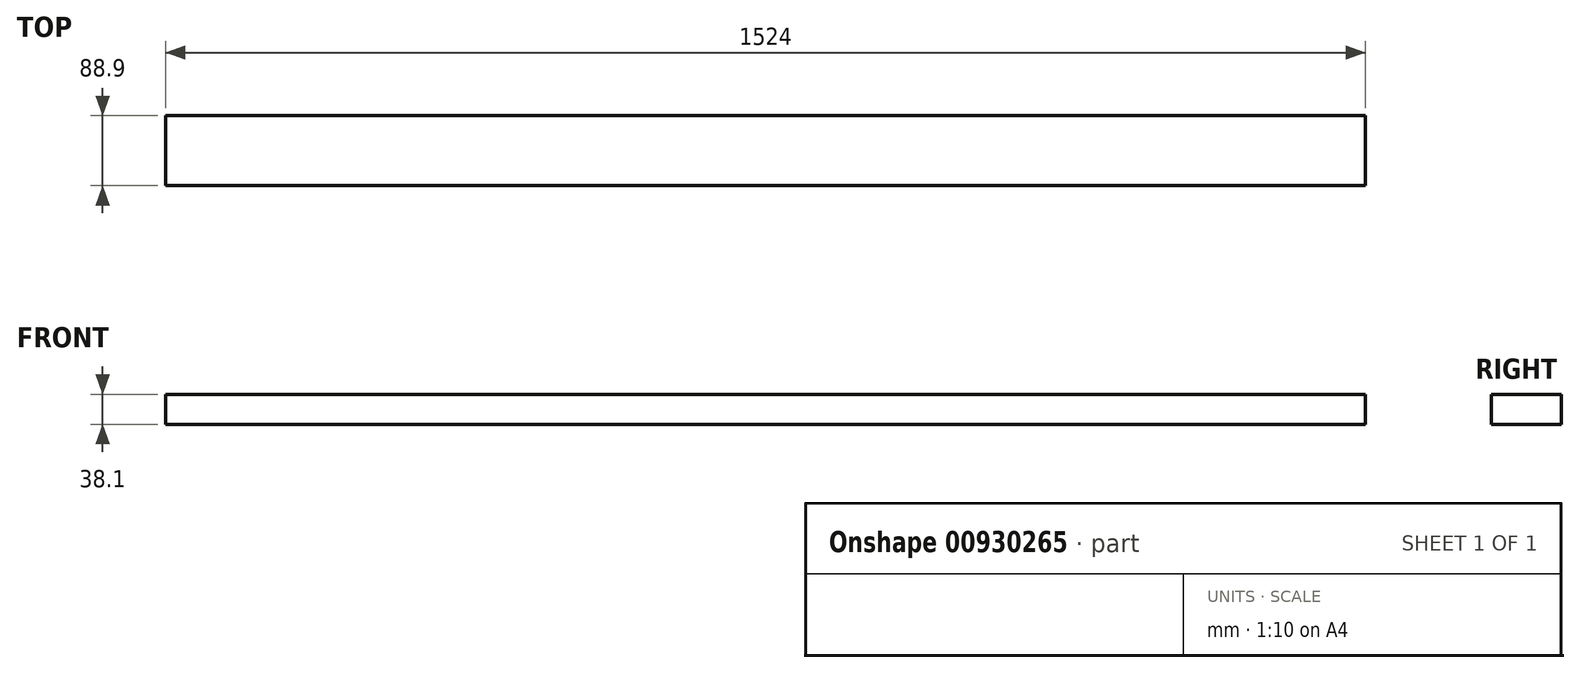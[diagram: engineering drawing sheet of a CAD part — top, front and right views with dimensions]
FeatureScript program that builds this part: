
annotation { "Feature Type Name" : "Feature", "Feature Type Description" : "" }
export const myFeature = defineFeature(function(context is Context, id is Id, definition is map)
    precondition{}
    {
        {
            var Q0;
            Q0=qCreatedBy(makeId("Right.planeOp"),FACE);
            var sketch = newSketch(context, id + "F0", { "sketchPlane" : qUnion([Q0])});
            skLineSegment(sketch, "E0.bottom", {"start": v(44.45, -19.05) * mm, "end": v(-44.45, -19.05) * mm});
            skLineSegment(sketch, "E0.top", {"start": v(44.45, 19.05) * mm, "end": v(-44.45, 19.05) * mm});
            skLineSegment(sketch, "E0.left", {"start": v(44.45, -19.05) * mm, "end": v(44.45, 19.05) * mm});
            skLineSegment(sketch, "E0.right", {"start": v(-44.45, -19.05) * mm, "end": v(-44.45, 19.05) * mm});
            skPoint(sketch, "E0.middle", {"position": v(0, 0) * mm});
            skSolve(sketch);
        }
        {
            var Q0;
            Q0=qSketchRegion(id+"F0",true);
            extrude(context, id + "F1", {"entities" : qUnion([Q0]), "endBound" : BoundingType.SYMMETRIC, "depth" : 1524 * mm});
        }
    });
